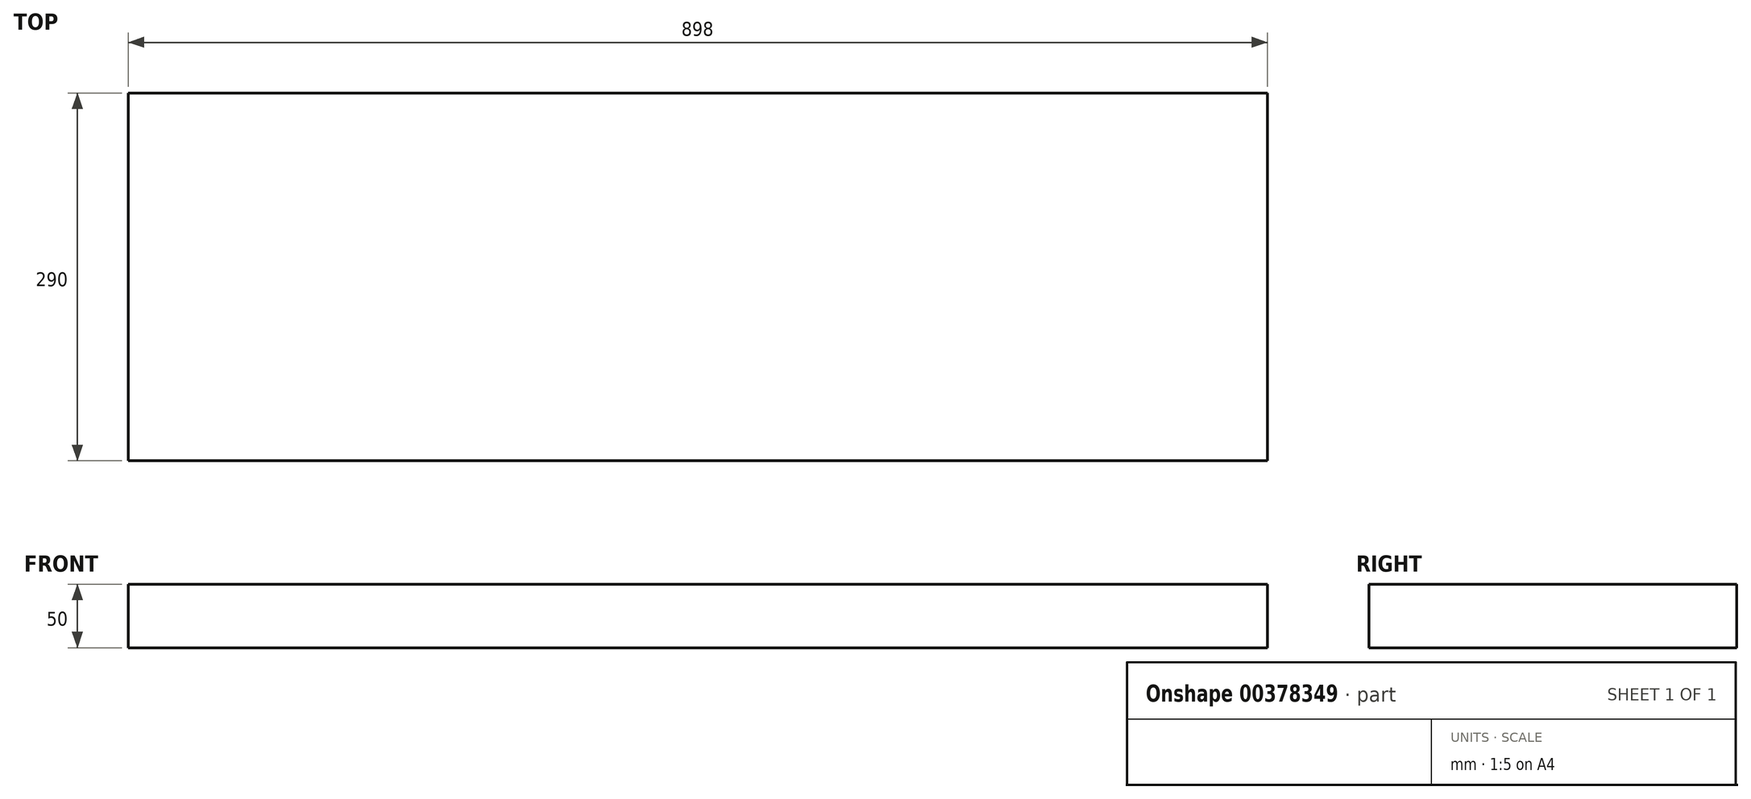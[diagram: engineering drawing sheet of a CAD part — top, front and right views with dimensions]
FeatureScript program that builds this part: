
annotation { "Feature Type Name" : "Feature", "Feature Type Description" : "" }
export const myFeature = defineFeature(function(context is Context, id is Id, definition is map)
    precondition{}
    {
        {
            var Q0;
            Q0=qCreatedBy(makeId("Top.planeOp"),FACE);
            var sketch = newSketch(context, id + "F0", { "sketchPlane" : qUnion([Q0])});
            skLineSegment(sketch, "E0.bottom", {"start": v(449, 145) * mm, "end": v(-449, 145) * mm});
            skLineSegment(sketch, "E0.top", {"start": v(449, -145) * mm, "end": v(-449, -145) * mm});
            skLineSegment(sketch, "E0.left", {"start": v(449, 145) * mm, "end": v(449, -145) * mm});
            skLineSegment(sketch, "E0.right", {"start": v(-449, 145) * mm, "end": v(-449, -145) * mm});
            skPoint(sketch, "E0.middle", {"position": v(0, 0) * mm});
            skSolve(sketch);
        }
        {
            var Q0;
            Q0 = qSketchRegion(id + "F0", true);
            extrude(context, id + "F1", {"entities" : qUnion([Q0]), "depth" : 50 * mm});
        }
    });
